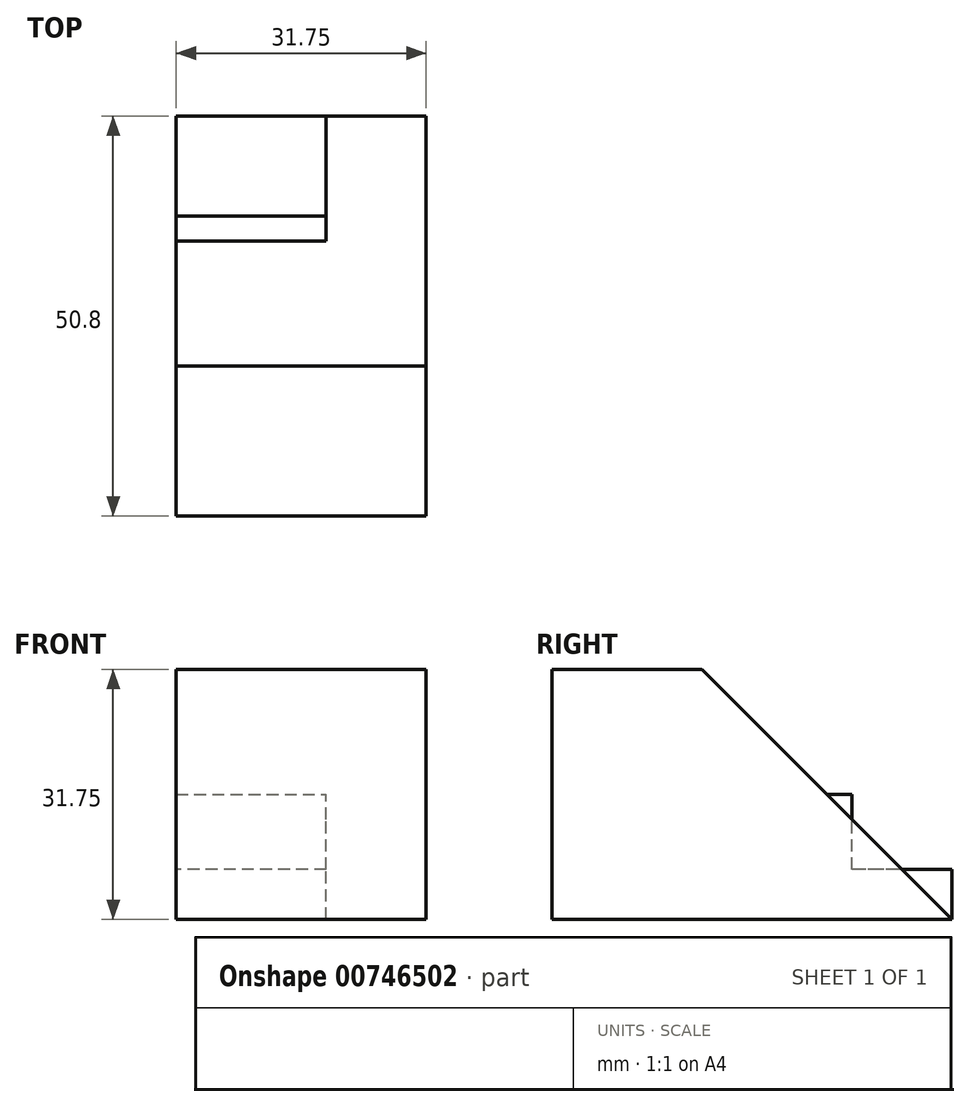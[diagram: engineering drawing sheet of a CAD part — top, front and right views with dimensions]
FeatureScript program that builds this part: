
annotation { "Feature Type Name" : "Feature", "Feature Type Description" : "" }
export const myFeature = defineFeature(function(context is Context, id is Id, definition is map)
    precondition{}
    {
        {
            var Q0;
            Q0=qCreatedBy(makeId("Right.planeOp"),FACE);
            var sketch = newSketch(context, id + "F0", { "sketchPlane" : qUnion([Q0])});
            skLineSegment(sketch, "E0", {"start": v(0, 0) * mm, "end": v(50.8, 0) * mm});
            skLineSegment(sketch, "E1", {"start": v(50.8, 0) * mm, "end": v(50.8, 31.75) * mm});
            skLineSegment(sketch, "E2", {"start": v(50.8, 31.75) * mm, "end": v(0, 31.75) * mm});
            skLineSegment(sketch, "E3", {"start": v(0, 31.75) * mm, "end": v(0, 0) * mm});
            skSolve(sketch);
        }
        {
            var Q0;
            Q0=makeQuery(id+"F0.imprint","IMPRINT",FACE,{"disambiguationData":[TD([[makeQuery(id+"F0.imprint","IMPRINT",EDGE,{"derivedFrom":sQuery(id+"F0.wireOp",EDGE,"E0")}),1.0]])]});
            extrude(context, id + "F1", {"entities" : qUnion([Q0]), "depth" : 31.75 * mm, "offsetDistance" : 25.4 * mm});
        }
        {
            var Q0;
            Q0=makeQuery(id+"F1.opExtrude","CAP_FACE",FACE,{"disambiguationData":[OSD([sQuery(id+"F0.wireOp",EDGE,"E0"),sQuery(id+"F0.wireOp",EDGE,"E1"),sQuery(id+"F0.wireOp",EDGE,"E2"),sQuery(id+"F0.wireOp",EDGE,"E3")])],"isStart":false});
            var sketch = newSketch(context, id + "F2", { "sketchPlane" : qUnion([Q0])});
            skLineSegment(sketch, "E4", {"start": v(50.8, 0) * mm, "end": v(19.05, 31.75) * mm});
            skLineSegment(sketch, "E5", {"start": v(19.05, 31.75) * mm, "end": v(50.8, 31.75) * mm});
            skLineSegment(sketch, "E6", {"start": v(50.8, 31.75) * mm, "end": v(50.8, 0) * mm});
            skSolve(sketch);
        }
        {
            var Q0;
            Q0=makeQuery(id+"F2.imprint","IMPRINT",FACE,{"disambiguationData":[TD([[makeQuery(id+"F2.imprint","IMPRINT",EDGE,{"derivedFrom":sQuery(id+"F2.wireOp",EDGE,"E4")}),-1.0]])]});
            extrude(context, id + "F3", {"entities" : qUnion([Q0]), "operationType" : NewBodyOperationType.REMOVE, "oppositeDirection" : true, "depth" : 12.7 * mm, "offsetDistance" : 25.4 * mm});
        }
        {
            var Q0;
            Q0=makeQuery(id+"F3.boolean.opBoolean","COPY",FACE,{"derivedFrom":makeQuery(id+"F3.opExtrude","CAP_FACE",FACE,{"disambiguationData":[OSD([sQuery(id+"F2.wireOp",EDGE,"E4"),sQuery(id+"F2.wireOp",EDGE,"E5"),sQuery(id+"F2.wireOp",EDGE,"E6")])],"isStart":false})});
            var sketch = newSketch(context, id + "F4", { "sketchPlane" : qUnion([Q0])});
            skLineSegment(sketch, "E7", {"start": v(34.92, 15.88) * mm, "end": v(38.1, 31.75) * mm});
            skLineSegment(sketch, "E8", {"start": v(38.1, 31.75) * mm, "end": v(19.05, 31.75) * mm});
            skLineSegment(sketch, "E9", {"start": v(19.05, 31.75) * mm, "end": v(34.92, 15.88) * mm});
            skSolve(sketch);
        }
        {
            var Q0;
            Q0=makeQuery(id+"F4.imprint","IMPRINT",FACE,{"disambiguationData":[TD([[makeQuery(id+"F4.imprint","IMPRINT",EDGE,{"derivedFrom":sQuery(id+"F4.wireOp",EDGE,"E7")}),1.0]])]});
            extrude(context, id + "F5", {"entities" : qUnion([Q0]), "operationType" : NewBodyOperationType.REMOVE, "oppositeDirection" : true, "depth" : 50.8 * mm, "offsetDistance" : 25.4 * mm});
        }
        {
            var Q0;
            Q0=makeQuery(id+"F3.boolean.opBoolean","COPY",FACE,{"derivedFrom":makeQuery(id+"F3.opExtrude","CAP_FACE",FACE,{"disambiguationData":[OSD([sQuery(id+"F2.wireOp",EDGE,"E4"),sQuery(id+"F2.wireOp",EDGE,"E5"),sQuery(id+"F2.wireOp",EDGE,"E6")])],"isStart":false})});
            var sketch = newSketch(context, id + "F6", { "sketchPlane" : qUnion([Q0])});
            skLineSegment(sketch, "E10", {"start": v(34.92, 15.88) * mm, "end": v(50.8, 15.88) * mm});
            skLineSegment(sketch, "E11", {"start": v(50.8, 15.88) * mm, "end": v(50.8, 31.75) * mm});
            skLineSegment(sketch, "E12", {"start": v(51.34, 31.2) * mm, "end": v(38.1, 31.75) * mm});
            skLineSegment(sketch, "E13", {"start": v(38.1, 31.75) * mm, "end": v(34.93, 15.88) * mm});
            skSolve(sketch);
        }
        {
            var Q0;
            {var subQ0=sQuery(id+"F6.wireOp",EDGE,"E10");Q0=makeQuery(id+"F6.imprint","IMPRINT",FACE,{"disambiguationData":[TD([[makeQuery(id+"F6.imprint","IMPRINT",EDGE,{"derivedFrom":subQ0}),1.0]])]});}
            extrude(context, id + "F7", {"entities" : qUnion([Q0]), "operationType" : NewBodyOperationType.REMOVE, "oppositeDirection" : true, "depth" : 25.4 * mm, "offsetDistance" : 25.4 * mm});
        }
        {
            var Q0;
            {var subQ0=sQuery(id+"F0.wireOp",EDGE,"E2");var subQ1=sQuery(id+"F0.wireOp",EDGE,"E1");Q0=makeQuery(id+"F5.boolean.opBoolean","SPLIT",FACE,{"disambiguationData":[TD([makeQuery(id+"F1.opExtrude","SWEPT_FACE",FACE,{"disambiguationData":[OSD([subQ1])]})])],"derivedFrom":makeQuery(id+"F1.opExtrude","SWEPT_FACE",FACE,{"disambiguationData":[OSD([subQ0])]})});}
            extrude(context, id + "F8", {"entities" : qUnion([Q0]), "operationType" : NewBodyOperationType.REMOVE, "oppositeDirection" : true, "depth" : 25.4 * mm, "offsetDistance" : 25.4 * mm});
        }
    });
